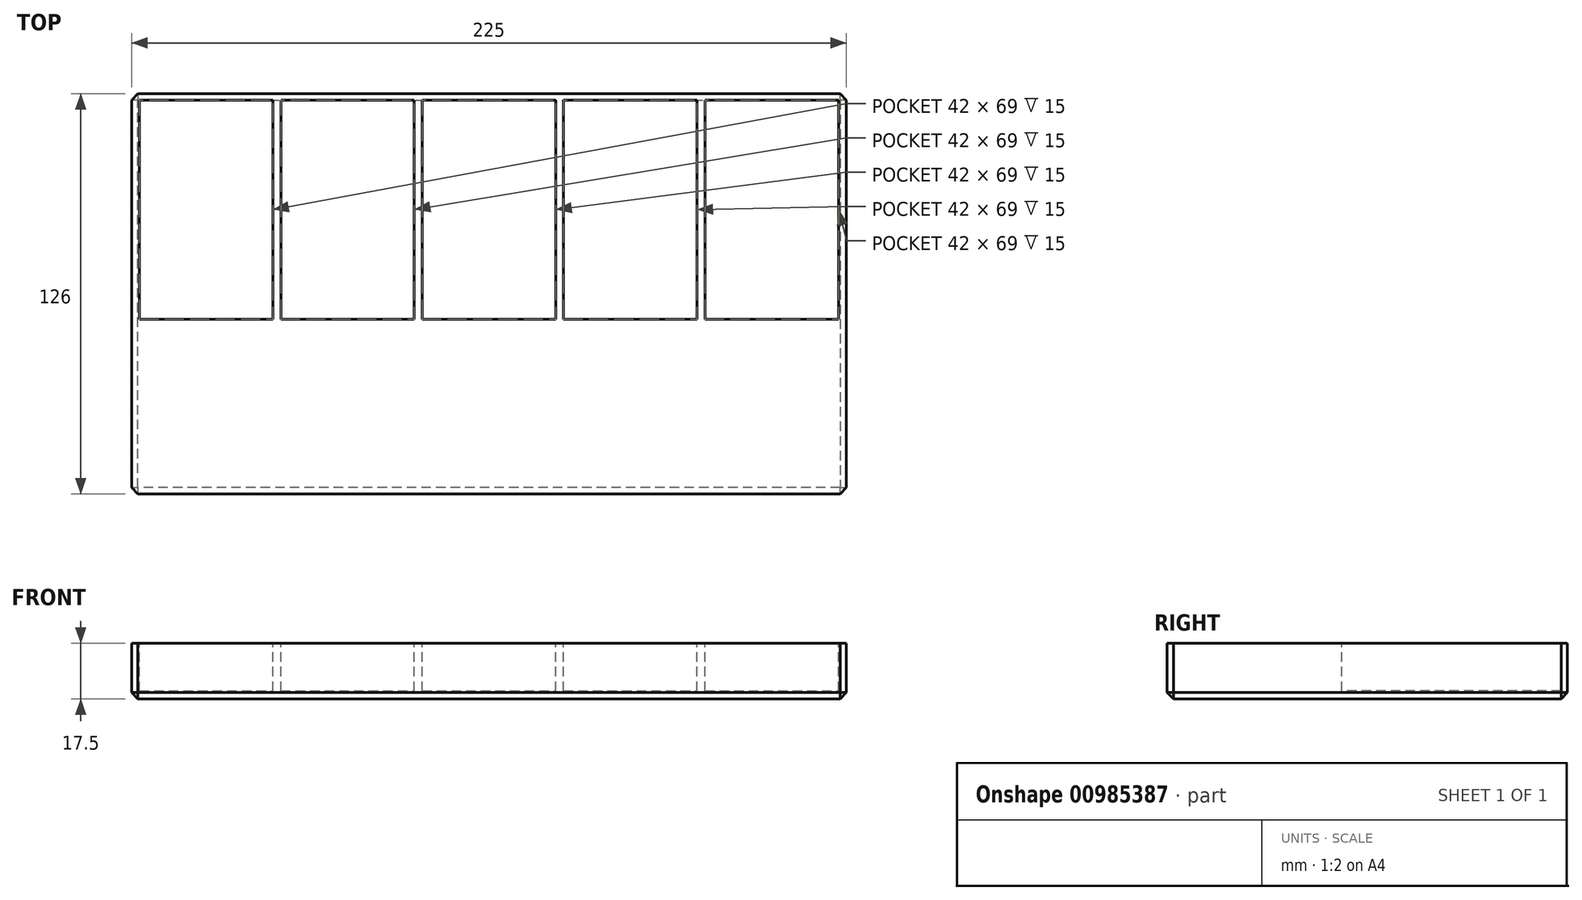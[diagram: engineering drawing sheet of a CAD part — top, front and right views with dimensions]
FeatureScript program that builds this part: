
annotation { "Feature Type Name" : "Feature", "Feature Type Description" : "" }
export const myFeature = defineFeature(function(context is Context, id is Id, definition is map)
    precondition{}
    {
        {
            var Q0;
            Q0=qCreatedBy(makeId("Top.planeOp"),FACE);
            var sketch = newSketch(context, id + "F0", { "sketchPlane" : qUnion([Q0])});
            skLineSegment(sketch, "E0.top", {"start": v(0, 63) * mm, "end": v(112.5, 63) * mm});
            skLineSegment(sketch, "E0.right", {"start": v(112.5, 0) * mm, "end": v(112.5, 63) * mm});
            skLineSegment(sketch, "E1.MirrorCS", {"start": v(0, 63) * mm, "end": v(-112.5, 63) * mm});
            skLineSegment(sketch, "E2.MirrorCS", {"start": v(-112.5, 0) * mm, "end": v(-112.5, 63) * mm});
            skLineSegment(sketch, "E3.MirrorCS", {"start": v(112.5, 0) * mm, "end": v(112.5, -63) * mm});
            skLineSegment(sketch, "E4.MirrorCS", {"start": v(0, -63) * mm, "end": v(112.5, -63) * mm});
            skLineSegment(sketch, "E5.MirrorCS", {"start": v(0, -63) * mm, "end": v(-112.5, -63) * mm});
            skLineSegment(sketch, "E6.MirrorCS", {"start": v(-112.5, 0) * mm, "end": v(-112.5, -63) * mm});
            skSolve(sketch);
        }
        {
            var Q0;
            Q0 = qSketchRegion(id + "F0", true);
            extrude(context, id + "F1", {"entities" : qUnion([Q0]), "depth" : 17.5 * mm, "offsetDistance" : 25 * mm});
        }
        {
            var Q0;
            Q0=makeQuery(id+"F1.opExtrude","CAP_EDGE",EDGE,{"disambiguationData":[OSD([sQuery(id+"F0.wireOp",EDGE,"E2.MirrorCS"),sQuery(id+"F0.wireOp",EDGE,"E6.MirrorCS")])],"isStart":true});
            var Q1;
            Q1=makeQuery(id+"F1.opExtrude","CAP_EDGE",EDGE,{"disambiguationData":[OSD([sQuery(id+"F0.wireOp",EDGE,"E4.MirrorCS"),sQuery(id+"F0.wireOp",EDGE,"E5.MirrorCS")])],"isStart":true});
            var Q2;
            Q2=makeQuery(id+"F1.opExtrude","CAP_EDGE",EDGE,{"disambiguationData":[OSD([sQuery(id+"F0.wireOp",EDGE,"E0.right"),sQuery(id+"F0.wireOp",EDGE,"E3.MirrorCS")])],"isStart":true});
            var Q3;
            Q3=makeQuery(id+"F1.opExtrude","CAP_EDGE",EDGE,{"disambiguationData":[OSD([sQuery(id+"F0.wireOp",EDGE,"E0.top"),sQuery(id+"F0.wireOp",EDGE,"E1.MirrorCS")])],"isStart":true});
            var Q4;
            Q4=makeQuery(id+"F1.opExtrude","SWEPT_EDGE",EDGE,{"disambiguationData":[OSD([sQuery(id+"F0.wireOp",EDGE,"E5.MirrorCS"),sQuery(id+"F0.wireOp",EDGE,"E6.MirrorCS")])]});
            var Q5;
            Q5=makeQuery(id+"F1.opExtrude","SWEPT_EDGE",EDGE,{"disambiguationData":[OSD([sQuery(id+"F0.wireOp",EDGE,"E3.MirrorCS"),sQuery(id+"F0.wireOp",EDGE,"E4.MirrorCS")])]});
            var Q6;
            Q6=makeQuery(id+"F1.opExtrude","SWEPT_EDGE",EDGE,{"disambiguationData":[OSD([sQuery(id+"F0.wireOp",EDGE,"E0.top"),sQuery(id+"F0.wireOp",EDGE,"E0.right")])]});
            var Q7;
            Q7=makeQuery(id+"F1.opExtrude","SWEPT_EDGE",EDGE,{"disambiguationData":[OSD([sQuery(id+"F0.wireOp",EDGE,"E1.MirrorCS"),sQuery(id+"F0.wireOp",EDGE,"E2.MirrorCS")])]});
            chamfer(context, id + "F2", {"entities" : qUnion([Q0, Q1, Q2, Q3, Q4, Q5, Q6, Q7]), "width" : 2 * mm, "tangentPropagation" : true});
        }
        {
            var Q0;
            Q0=makeQuery(id+"F1.opExtrude","CAP_FACE",FACE,{"disambiguationData":[OSD([sQuery(id+"F0.wireOp",EDGE,"E0.top"),sQuery(id+"F0.wireOp",EDGE,"E0.right"),sQuery(id+"F0.wireOp",EDGE,"E1.MirrorCS"),sQuery(id+"F0.wireOp",EDGE,"E2.MirrorCS"),sQuery(id+"F0.wireOp",EDGE,"E3.MirrorCS"),sQuery(id+"F0.wireOp",EDGE,"E4.MirrorCS"),sQuery(id+"F0.wireOp",EDGE,"E5.MirrorCS"),sQuery(id+"F0.wireOp",EDGE,"E6.MirrorCS")])],"isStart":false});
            var sketch = newSketch(context, id + "F3", { "sketchPlane" : qUnion([Q0])});
            skLineSegment(sketch, "E7.bottom", {"start": v(68, 61) * mm, "end": v(110, 61) * mm});
            skLineSegment(sketch, "E7.top", {"start": v(68, -8) * mm, "end": v(110, -8) * mm});
            skLineSegment(sketch, "E7.left", {"start": v(68, 61) * mm, "end": v(68, -8) * mm});
            skLineSegment(sketch, "E7.right", {"start": v(110, 61) * mm, "end": v(110, -8) * mm});
            skLineSegment(sketch, "E8", {"start": v(0, 63) * mm, "end": v(110.5, 63) * mm, "construction": true});
            skLineSegment(sketch, "E9", {"start": v(112.5, 61) * mm, "end": v(112.5, 0) * mm, "construction": true});
            skLineSegment(sketch, "E10.bottom", {"start": v(23.5, 61) * mm, "end": v(65.5, 61) * mm});
            skLineSegment(sketch, "E10.top", {"start": v(23.5, -8) * mm, "end": v(65.5, -8) * mm});
            skLineSegment(sketch, "E10.left", {"start": v(23.5, 61) * mm, "end": v(23.5, -8) * mm});
            skLineSegment(sketch, "E10.right", {"start": v(65.5, 61) * mm, "end": v(65.5, -8) * mm});
            skLineSegment(sketch, "E11.bottom", {"start": v(-21, 61) * mm, "end": v(21, 61) * mm});
            skLineSegment(sketch, "E11.top", {"start": v(-21, -8) * mm, "end": v(21, -8) * mm});
            skLineSegment(sketch, "E11.left", {"start": v(-21, 61) * mm, "end": v(-21, -8) * mm});
            skLineSegment(sketch, "E11.right", {"start": v(21, 61) * mm, "end": v(21, -8) * mm});
            skLineSegment(sketch, "E12.bottom", {"start": v(-65.5, 61) * mm, "end": v(-23.5, 61) * mm});
            skLineSegment(sketch, "E12.top", {"start": v(-65.5, -8) * mm, "end": v(-23.5, -8) * mm});
            skLineSegment(sketch, "E12.left", {"start": v(-65.5, 61) * mm, "end": v(-65.5, -8) * mm});
            skLineSegment(sketch, "E12.right", {"start": v(-23.5, 61) * mm, "end": v(-23.5, -8) * mm});
            skLineSegment(sketch, "E13.bottom", {"start": v(-110, 61) * mm, "end": v(-68, 61) * mm});
            skLineSegment(sketch, "E13.top", {"start": v(-110, -8) * mm, "end": v(-68, -8) * mm});
            skLineSegment(sketch, "E13.left", {"start": v(-110, 61) * mm, "end": v(-110, -8) * mm});
            skLineSegment(sketch, "E13.right", {"start": v(-68, 61) * mm, "end": v(-68, -8) * mm});
            skSolve(sketch);
        }
        {
            var Q0;
            Q0 = qSketchRegion(id + "F3", true);
            extrude(context, id + "F4", {"entities" : qUnion([Q0]), "operationType" : NewBodyOperationType.REMOVE, "oppositeDirection" : true, "depth" : 15 * mm, "offsetDistance" : 25 * mm});
        }
    });
